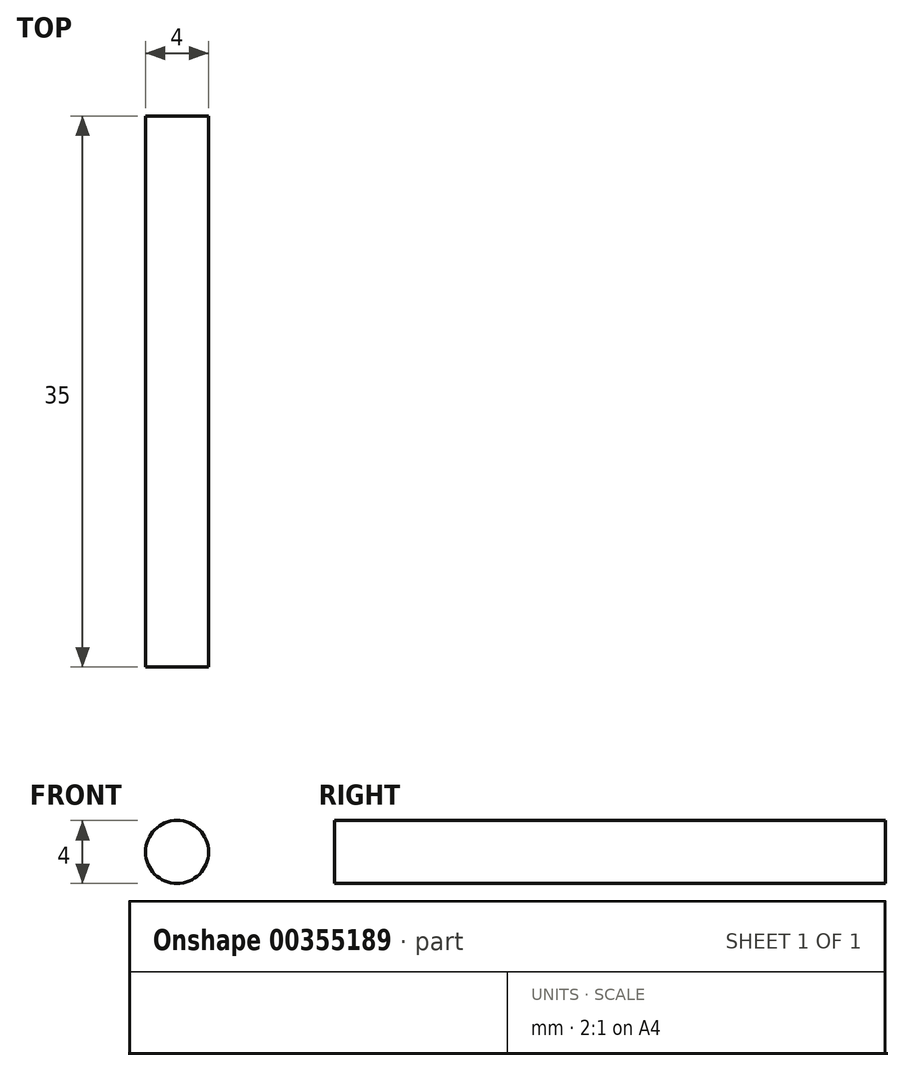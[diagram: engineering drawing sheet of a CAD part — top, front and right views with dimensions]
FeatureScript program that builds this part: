
annotation { "Feature Type Name" : "Feature", "Feature Type Description" : "" }
export const myFeature = defineFeature(function(context is Context, id is Id, definition is map)
    precondition{}
    {
        {
            var Q0;
            Q0=qCreatedBy(makeId("Front.planeOp"),FACE);
            var sketch = newSketch(context, id + "F0", { "sketchPlane" : qUnion([Q0])});
            skCircle(sketch, "E0", {"center": v(0, 2.08) * mm, "radius": 2 * mm});
            skSolve(sketch);
        }
        {
            var Q0;
            Q0=makeQuery(id+"F0.imprint","IMPRINT",FACE,{"disambiguationData":[TD([[makeQuery(id+"F0.imprint","IMPRINT",EDGE,{"derivedFrom":sQuery(id+"F0.wireOp",EDGE,"E0")}),1.0]])]});
            extrude(context, id + "F1", {"entities" : qUnion([Q0]), "depth" : 35 * mm});
        }
    });
